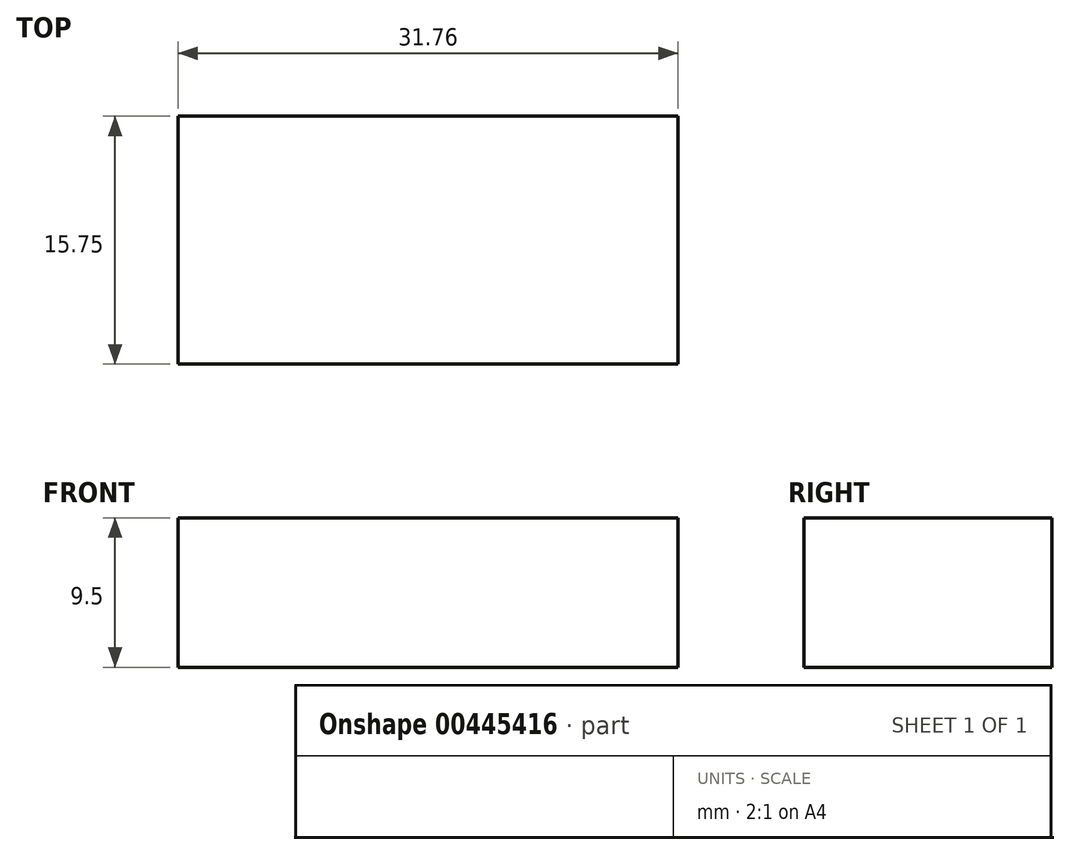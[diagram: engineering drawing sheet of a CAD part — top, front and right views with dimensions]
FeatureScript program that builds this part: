
annotation { "Feature Type Name" : "Feature", "Feature Type Description" : "" }
export const myFeature = defineFeature(function(context is Context, id is Id, definition is map)
    precondition{}
    {
        {
            var Q0;
            Q0=qCreatedBy(makeId("Top.planeOp"),FACE);
            var sketch = newSketch(context, id + "F0", { "sketchPlane" : qUnion([Q0])});
            skLineSegment(sketch, "E0.bottom", {"start": v(15.88, 7) * mm, "end": v(-15.88, 7) * mm});
            skLineSegment(sketch, "E0.top", {"start": v(15.88, -8.75) * mm, "end": v(-15.88, -8.75) * mm});
            skLineSegment(sketch, "E0.left", {"start": v(15.88, 7) * mm, "end": v(15.88, -8.75) * mm});
            skLineSegment(sketch, "E0.right", {"start": v(-15.88, 7) * mm, "end": v(-15.88, -8.75) * mm});
            skPoint(sketch, "E0.middle", {"position": v(0, -0.88) * mm});
            skSolve(sketch);
        }
        {
            var Q0;
            Q0 = qSketchRegion(id + "F0", true);
            extrude(context, id + "F1", {"entities" : qUnion([Q0]), "depth" : 9.5 * mm});
        }
    });
